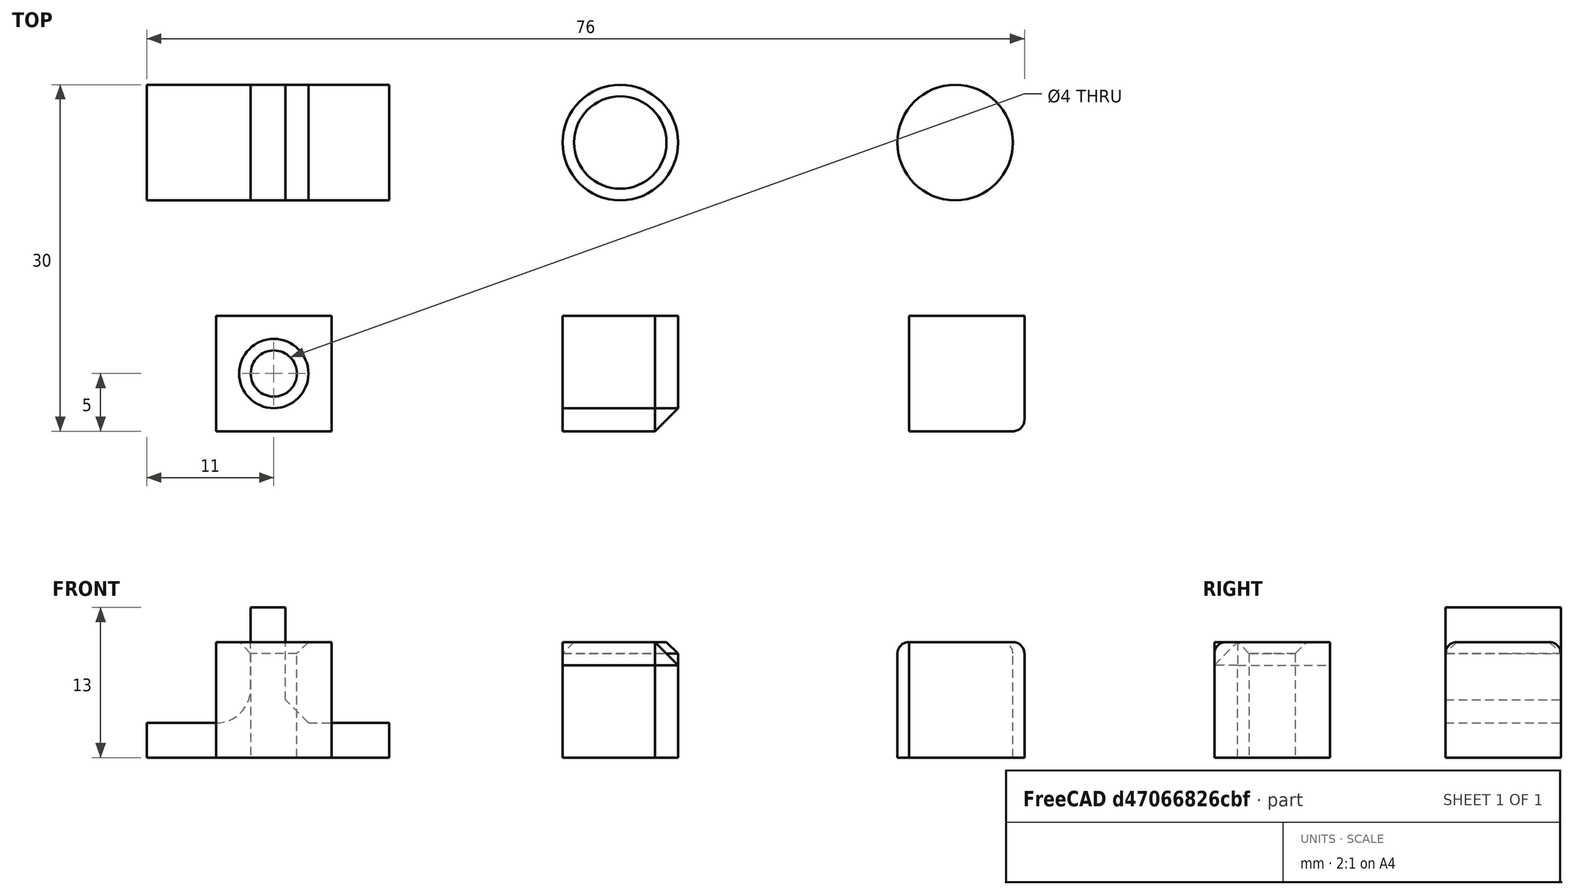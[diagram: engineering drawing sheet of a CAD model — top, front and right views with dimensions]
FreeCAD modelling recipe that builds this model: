
FCSTD DOCUMENT  (FreeCAD 0.21R33771 (Git))
Label: OJT1_T12P01_arrodoniments_xamfrans_reforços
License: All rights reserved
LicenseURL: http://en.wikipedia.org/wiki/All_rights_reserved
objects: Part::Box×5, Part::Chamfer×4, Part::Cylinder×3, Part::Fillet×3, Part::MultiFuse×1, Part::Cut×1
note: 17 computed .brp shape members not serialized (recipe doc carries the construction recipe); baked Part::Feature solids carry a one-line shape summary decoded from their .brp

FEATURE [Part::Box] Box  label="Cube"
  AttacherType = Attacher::AttachEngine3D
  Height = 10
  Length = 10
  Width = 10
FEATURE [Part::Box] Box001  label="Cube001"
  AttacherType = Attacher::AttachEngine3D
  Height = 10
  Length = 10
  Placement = pos=(30,0,0) rot=(0,0,1;0rad)
  Width = 10
FEATURE [Part::Box] Box002  label="Cube002"
  AttacherType = Attacher::AttachEngine3D
  Height = 10
  Length = 10
  Placement = pos=(60,0,0) rot=(0,0,1;0rad)
  Width = 10
FEATURE [Part::Box] Box003  label="Cube003"
  AttacherType = Attacher::AttachEngine3D
  Height = 3
  Length = 21
  Placement = pos=(-6,20,0) rot=(0,0,1;0rad)
  Width = 10
FEATURE [Part::Box] Box004  label="Cube004"
  AttacherType = Attacher::AttachEngine3D
  Height = 10
  Length = 3
  Placement = pos=(3,20,3) rot=(0,0,1;0rad)
  Width = 10
FEATURE [Part::MultiFuse] Fusion
  Refine = true
  Shapes = -> [Box003,Box004]
FEATURE [Part::Cylinder] Cylinder
  Angle = 360
  AttacherType = Attacher::AttachEngine3D
  FirstAngle = 0
  Height = 10
  Placement = pos=(64,25,0) rot=(0,0,1;0rad)
  Radius = 5
  SecondAngle = 0
FEATURE [Part::Cylinder] Cylinder001
  Angle = 360
  AttacherType = Attacher::AttachEngine3D
  FirstAngle = 0
  Height = 10
  Placement = pos=(35,25,0) rot=(0,0,1;0rad)
  Radius = 5
  SecondAngle = 0
FEATURE [Part::Cylinder] Cylinder002
  Angle = 360
  AttacherType = Attacher::AttachEngine3D
  FirstAngle = 0
  Height = 12
  Placement = pos=(5,5,-1) rot=(0,0,1;0rad)
  Radius = 2
  SecondAngle = 0
FEATURE [Part::Cut] Cut
  Base = -> Box
  Refine = true
  Tool = -> Cylinder002
FEATURE [Part::Fillet] Fillet  label="cantell_rodo"
  Base = -> Box002
  Edges = 3 edges r=1: [Edge5,Edge6,Edge10]
FEATURE [Part::Chamfer] Chamfer
  Base = -> Box001
  Edges = 3 edges r=2: [Edge5,Edge6,Edge10]
FEATURE [Part::Chamfer] Chamfer001
  Base = -> Cut
  Edges = 1 edges r=1: [Edge10]
FEATURE [Part::Fillet] Fillet001
  Base = -> Cylinder
  Edges = 1 edges r=1: [Edge3]
FEATURE [Part::Chamfer] Chamfer002
  Base = -> Cylinder001
  Edges = 1 edges r=1: [Edge3]
FEATURE [Part::Chamfer] Chamfer003
  Base = -> Fusion
  Edges = 1 edges r=2: [Edge16]
FEATURE [Part::Fillet] Fillet002  label="reforços"
  Base = -> Chamfer003
  Edges = 1 edges r=3: [Edge25]
